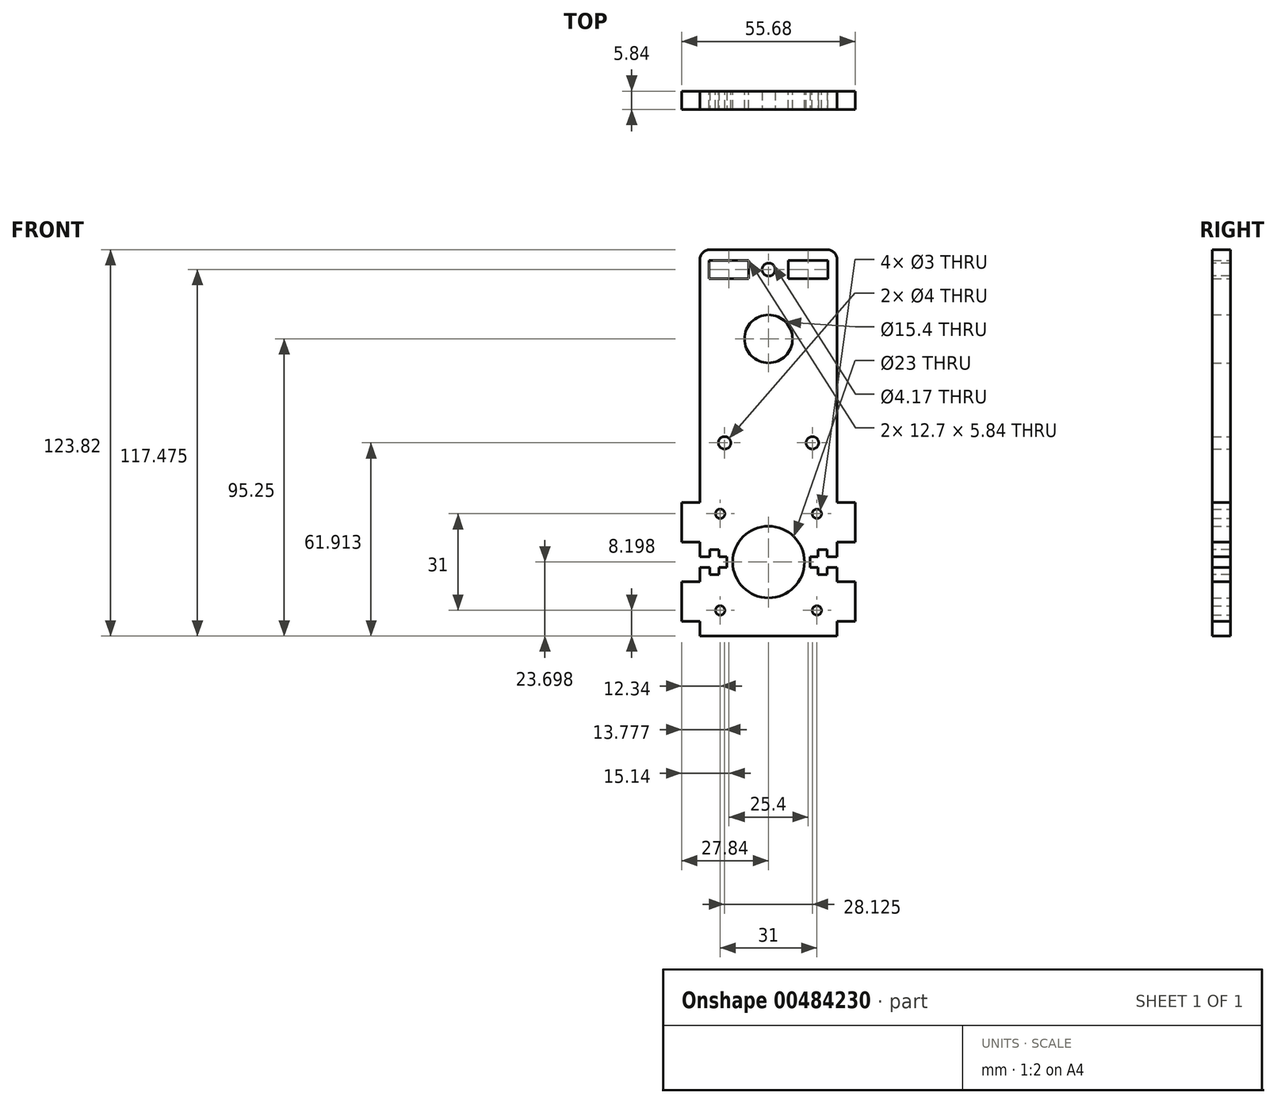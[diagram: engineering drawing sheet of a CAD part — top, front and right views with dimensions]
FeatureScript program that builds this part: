
annotation { "Feature Type Name" : "Feature", "Feature Type Description" : "" }
export const myFeature = defineFeature(function(context is Context, id is Id, definition is map)
    precondition{}
    {
        {
            var Q0;
            Q0=qCreatedBy(makeId("Front.planeOp"),FACE);
            var sketch = newSketch(context, id + "F0", { "sketchPlane" : qUnion([Q0])});
            skCircle(sketch, "E0", {"center": v(0, 0) * mm, "radius": 7.7 * mm});
            skCircle(sketch, "E1", {"center": v(0, 0) * mm, "radius": 8 * mm, "construction": true});
            skCircle(sketch, "E2", {"center": v(0, -71.55) * mm, "radius": 11.5 * mm});
            skLineSegment(sketch, "E3.bottom", {"start": v(-22, 28.58) * mm, "end": v(22, 28.58) * mm});
            skLineSegment(sketch, "E3.top", {"start": v(-22, -95.25) * mm, "end": v(22, -95.25) * mm});
            skLineSegment(sketch, "E3.right", {"start": v(22, 28.58) * mm, "end": v(22, -52.5) * mm});
            skPoint(sketch, "E3.middle", {"position": v(0, -33.34) * mm});
            skCircle(sketch, "E4", {"center": v(0, 0) * mm, "radius": 15.88 * mm, "construction": true});
            skLineSegment(sketch, "E5.bottom", {"start": v(-21.15, -50.4) * mm, "end": v(21.15, -50.4) * mm, "construction": true});
            skLineSegment(sketch, "E5.top", {"start": v(-21.15, -92.7) * mm, "end": v(21.15, -92.7) * mm, "construction": true});
            skLineSegment(sketch, "E5.left", {"start": v(-21.15, -50.4) * mm, "end": v(-21.15, -92.7) * mm, "construction": true});
            skLineSegment(sketch, "E5.right", {"start": v(21.15, -50.4) * mm, "end": v(21.15, -92.7) * mm, "construction": true});
            skLineSegment(sketch, "E6", {"start": v(-15.85, -0.97) * mm, "end": v(-11.48, -72.25) * mm, "construction": true});
            skLineSegment(sketch, "E7", {"start": v(0, 0) * mm, "end": v(0, -71.55) * mm, "construction": true});
            skLineSegment(sketch, "E8.MirrorCS", {"start": v(15.85, -0.97) * mm, "end": v(11.48, -72.25) * mm, "construction": true});
            skLineSegment(sketch, "E9", {"start": v(-21.15, -71.55) * mm, "end": v(21.15, -71.55) * mm, "construction": true});
            skLineSegment(sketch, "E10", {"start": v(0, -92.7) * mm, "end": v(0, -50.4) * mm, "construction": true});
            skCircle(sketch, "E11", {"center": v(-15.5, -56.05) * mm, "radius": 1.5 * mm});
            skCircle(sketch, "E12.MirrorC", {"center": v(15.5, -56.05) * mm, "radius": 1.5 * mm});
            skCircle(sketch, "E13.MirrorC", {"center": v(15.5, -87.05) * mm, "radius": 1.5 * mm});
            skCircle(sketch, "E14.MirrorC", {"center": v(-15.5, -87.05) * mm, "radius": 1.5 * mm});
            skLineSegment(sketch, "E15.bottom", {"start": v(-22, -77.9) * mm, "end": v(-27.84, -77.9) * mm});
            skLineSegment(sketch, "E15.top", {"start": v(-22, -90.6) * mm, "end": v(-27.84, -90.6) * mm});
            skLineSegment(sketch, "E15.right", {"start": v(-27.84, -77.9) * mm, "end": v(-27.84, -90.6) * mm});
            skPoint(sketch, "E15.middle", {"position": v(-24.92, -84.25) * mm});
            skLineSegment(sketch, "E16.MirrorCS", {"start": v(-22, -65.2) * mm, "end": v(-27.84, -65.2) * mm});
            skLineSegment(sketch, "E17.MirrorCS", {"start": v(-27.84, -65.2) * mm, "end": v(-27.84, -52.5) * mm});
            skLineSegment(sketch, "E18.MirrorCS", {"start": v(-22, -52.5) * mm, "end": v(-27.84, -52.5) * mm});
            skLineSegment(sketch, "E19.trimOffspring", {"start": v(-22, -65.2) * mm, "end": v(-22, -77.9) * mm});
            skLineSegment(sketch, "E20.trimOffspring", {"start": v(-22, -90.6) * mm, "end": v(-22, -95.25) * mm});
            skLineSegment(sketch, "E21", {"start": v(-22, -52.5) * mm, "end": v(-22, 28.58) * mm});
            skLineSegment(sketch, "E22.bottom", {"start": v(-6.35, 25.15) * mm, "end": v(-19.05, 25.15) * mm});
            skLineSegment(sketch, "E22.top", {"start": v(-6.35, 19.3) * mm, "end": v(-19.05, 19.3) * mm});
            skLineSegment(sketch, "E22.left", {"start": v(-6.35, 25.15) * mm, "end": v(-6.35, 19.3) * mm});
            skLineSegment(sketch, "E22.right", {"start": v(-19.05, 25.15) * mm, "end": v(-19.05, 19.3) * mm});
            skPoint(sketch, "E22.middle", {"position": v(-12.7, 22.23) * mm});
            skLineSegment(sketch, "E23.MirrorCS", {"start": v(6.35, 25.15) * mm, "end": v(6.35, 19.3) * mm});
            skLineSegment(sketch, "E24.MirrorCS", {"start": v(6.35, 25.15) * mm, "end": v(19.05, 25.15) * mm});
            skLineSegment(sketch, "E25.MirrorCS", {"start": v(19.05, 25.15) * mm, "end": v(19.05, 19.3) * mm});
            skLineSegment(sketch, "E26.MirrorCS", {"start": v(6.35, 19.3) * mm, "end": v(19.05, 19.3) * mm});
            skLineSegment(sketch, "E27.MirrorCS", {"start": v(22, -52.5) * mm, "end": v(27.84, -52.5) * mm});
            skLineSegment(sketch, "E28.MirrorCS", {"start": v(27.84, -65.2) * mm, "end": v(27.84, -52.5) * mm});
            skLineSegment(sketch, "E29.MirrorCS", {"start": v(22, -77.9) * mm, "end": v(27.84, -77.9) * mm});
            skLineSegment(sketch, "E30.MirrorCS", {"start": v(27.84, -77.9) * mm, "end": v(27.84, -90.6) * mm});
            skLineSegment(sketch, "E31.MirrorCS", {"start": v(22, -90.6) * mm, "end": v(27.84, -90.6) * mm});
            skLineSegment(sketch, "E32", {"start": v(27.84, -65.2) * mm, "end": v(22, -65.2) * mm});
            skLineSegment(sketch, "E33.trimOffspring", {"start": v(22, -65.2) * mm, "end": v(22, -77.9) * mm});
            skLineSegment(sketch, "E34.trimOffspring", {"start": v(22, -90.6) * mm, "end": v(22, -95.25) * mm});
            skLineSegment(sketch, "E35", {"start": v(0, -33.34) * mm, "end": v(22, -33.34) * mm, "construction": true});
            skLineSegment(sketch, "E36", {"start": v(0, -33.34) * mm, "end": v(-22, -33.34) * mm, "construction": true});
            skCircle(sketch, "E37", {"center": v(-14.06, -33.34) * mm, "radius": 2 * mm});
            skPoint(sketch, "E38", {"position": v(-13.86, -33.34) * mm});
            skCircle(sketch, "E39.MirrorC", {"center": v(14.06, -33.34) * mm, "radius": 2 * mm});
            skSolve(sketch);
        }
        {
            var Q0;
            Q0 = qSketchRegion(id + "F0", true);
            extrude(context, id + "F1", {"entities" : qUnion([Q0]), "depth" : 5.84 * mm});
        }
        {
            var Q0;
            Q0=makeQuery(id+"F1.opExtrude","SWEPT_EDGE",EDGE,{"disambiguationData":[OSD([sQuery(id+"F0.wireOp",EDGE,"E3.bottom"),sQuery(id+"F0.wireOp",EDGE,"E21")])]});
            var Q1;
            Q1=makeQuery(id+"F1.opExtrude","SWEPT_EDGE",EDGE,{"disambiguationData":[OSD([sQuery(id+"F0.wireOp",EDGE,"E3.bottom"),sQuery(id+"F0.wireOp",EDGE,"E3.right")])]});
            fillet(context, id + "F2", {"entities" : qUnion([Q0, Q1]), "radius" : 3.17 * mm, "tangentPropagation" : true, "allowEdgeOverflow" : false});
        }
        {
            var Q0;
            Q0=makeQuery(id+"F1.opExtrude","CAP_FACE",FACE,{"disambiguationData":[OSD([sQuery(id+"F0.wireOp",EDGE,"E0"),sQuery(id+"F0.wireOp",EDGE,"E2"),sQuery(id+"F0.wireOp",EDGE,"E3.bottom"),sQuery(id+"F0.wireOp",EDGE,"E3.top"),sQuery(id+"F0.wireOp",EDGE,"E3.right"),sQuery(id+"F0.wireOp",EDGE,"E12.MirrorC"),sQuery(id+"F0.wireOp",EDGE,"E11"),sQuery(id+"F0.wireOp",EDGE,"E13.MirrorC"),sQuery(id+"F0.wireOp",EDGE,"E14.MirrorC"),sQuery(id+"F0.wireOp",EDGE,"E15.bottom"),sQuery(id+"F0.wireOp",EDGE,"E15.top"),sQuery(id+"F0.wireOp",EDGE,"E15.right"),sQuery(id+"F0.wireOp",EDGE,"E16.MirrorCS"),sQuery(id+"F0.wireOp",EDGE,"E17.MirrorCS"),sQuery(id+"F0.wireOp",EDGE,"E18.MirrorCS"),sQuery(id+"F0.wireOp",EDGE,"E19.trimOffspring"),sQuery(id+"F0.wireOp",EDGE,"E20.trimOffspring"),sQuery(id+"F0.wireOp",EDGE,"E21"),sQuery(id+"F0.wireOp",EDGE,"E22.bottom"),sQuery(id+"F0.wireOp",EDGE,"E22.top"),sQuery(id+"F0.wireOp",EDGE,"E22.left"),sQuery(id+"F0.wireOp",EDGE,"E22.right"),sQuery(id+"F0.wireOp",EDGE,"E23.MirrorCS"),sQuery(id+"F0.wireOp",EDGE,"E24.MirrorCS"),sQuery(id+"F0.wireOp",EDGE,"E25.MirrorCS"),sQuery(id+"F0.wireOp",EDGE,"E26.MirrorCS"),sQuery(id+"F0.wireOp",EDGE,"E27.MirrorCS"),sQuery(id+"F0.wireOp",EDGE,"E28.MirrorCS"),sQuery(id+"F0.wireOp",EDGE,"E29.MirrorCS"),sQuery(id+"F0.wireOp",EDGE,"E30.MirrorCS"),sQuery(id+"F0.wireOp",EDGE,"E31.MirrorCS"),sQuery(id+"F0.wireOp",EDGE,"E32"),sQuery(id+"F0.wireOp",EDGE,"E33.trimOffspring"),sQuery(id+"F0.wireOp",EDGE,"E34.trimOffspring"),sQuery(id+"F0.wireOp",EDGE,"E37"),sQuery(id+"F0.wireOp",EDGE,"E39.MirrorC")])],"isStart":false});
            var sketch = newSketch(context, id + "F3", { "sketchPlane" : qUnion([Q0])});
            skLineSegment(sketch, "E40", {"start": v(-22, -71.55) * mm, "end": v(22, -71.55) * mm, "construction": true});
            skLineSegment(sketch, "E41.bottom", {"start": v(-22, -69.8) * mm, "end": v(-18.83, -69.8) * mm});
            skLineSegment(sketch, "E41.top", {"start": v(-22, -73.3) * mm, "end": v(-18.83, -73.3) * mm});
            skLineSegment(sketch, "E41.left", {"start": v(-22, -69.8) * mm, "end": v(-22, -73.3) * mm});
            skPoint(sketch, "E41.middle", {"position": v(-20.41, -71.55) * mm});
            skLineSegment(sketch, "E42.bottom", {"start": v(-18.83, -67.58) * mm, "end": v(-15.85, -67.58) * mm});
            skLineSegment(sketch, "E42.top", {"start": v(-18.83, -75.52) * mm, "end": v(-15.85, -75.52) * mm});
            skLineSegment(sketch, "E42.left", {"start": v(-18.83, -67.58) * mm, "end": v(-18.83, -69.8) * mm});
            skLineSegment(sketch, "E42.right", {"start": v(-15.85, -67.58) * mm, "end": v(-15.85, -69.8) * mm});
            skPoint(sketch, "E42.middle", {"position": v(-17.34, -71.55) * mm});
            skLineSegment(sketch, "E43.trimOffspring", {"start": v(-18.83, -73.3) * mm, "end": v(-18.83, -75.52) * mm});
            skLineSegment(sketch, "E44.bottom", {"start": v(-15.85, -69.8) * mm, "end": v(-13.35, -69.8) * mm});
            skLineSegment(sketch, "E44.top", {"start": v(-15.85, -73.3) * mm, "end": v(-13.35, -73.3) * mm});
            skLineSegment(sketch, "E44.right", {"start": v(-13.35, -69.8) * mm, "end": v(-13.35, -73.3) * mm});
            skPoint(sketch, "E44.middle", {"position": v(-14.6, -71.55) * mm});
            skLineSegment(sketch, "E45.trimOffspring", {"start": v(-15.85, -73.3) * mm, "end": v(-15.85, -75.52) * mm});
            skLineSegment(sketch, "E46", {"start": v(0, -54.52) * mm, "end": v(0, -71.55) * mm, "construction": true});
            skLineSegment(sketch, "E47.MirrorCS", {"start": v(22, -69.8) * mm, "end": v(18.82, -69.8) * mm});
            skLineSegment(sketch, "E48.MirrorCS", {"start": v(22, -73.3) * mm, "end": v(18.82, -73.3) * mm});
            skPoint(sketch, "E49.MirrorP", {"position": v(14.6, -71.55) * mm});
            skLineSegment(sketch, "E50.MirrorCS", {"start": v(22, -69.8) * mm, "end": v(22, -73.3) * mm});
            skLineSegment(sketch, "E51.MirrorCS", {"start": v(18.82, -67.58) * mm, "end": v(15.85, -67.58) * mm});
            skLineSegment(sketch, "E52.MirrorCS", {"start": v(18.82, -75.52) * mm, "end": v(15.85, -75.52) * mm});
            skLineSegment(sketch, "E53.MirrorCS", {"start": v(15.85, -67.58) * mm, "end": v(15.85, -69.8) * mm});
            skLineSegment(sketch, "E54.MirrorCS", {"start": v(18.82, -73.3) * mm, "end": v(18.82, -75.52) * mm});
            skLineSegment(sketch, "E55.MirrorCS", {"start": v(15.85, -69.8) * mm, "end": v(13.35, -69.8) * mm});
            skLineSegment(sketch, "E56.MirrorCS", {"start": v(22, -71.55) * mm, "end": v(-22, -71.55) * mm, "construction": true});
            skPoint(sketch, "E57.MirrorP", {"position": v(17.34, -71.55) * mm});
            skLineSegment(sketch, "E58.MirrorCS", {"start": v(18.82, -67.58) * mm, "end": v(18.82, -69.8) * mm});
            skPoint(sketch, "E59.MirrorP", {"position": v(20.41, -71.55) * mm});
            skLineSegment(sketch, "E60.MirrorCS", {"start": v(15.85, -73.3) * mm, "end": v(13.35, -73.3) * mm});
            skLineSegment(sketch, "E61.MirrorCS", {"start": v(15.85, -73.3) * mm, "end": v(15.85, -75.52) * mm});
            skLineSegment(sketch, "E62.MirrorCS", {"start": v(13.35, -69.8) * mm, "end": v(13.35, -73.3) * mm});
            skSolve(sketch);
        }
        {
            var Q0;
            Q0 = qSketchRegion(id + "F3", true);
            extrude(context, id + "F4", {"entities" : qUnion([Q0]), "operationType" : NewBodyOperationType.REMOVE, "endBound" : BoundingType.THROUGH_ALL, "oppositeDirection" : true, "depth" : 25.4 * mm});
        }
        {
            var Q0;
            Q0=makeQuery(id+"F1.opExtrude","CAP_FACE",FACE,{"disambiguationData":[OSD([sQuery(id+"F0.wireOp",EDGE,"E0"),sQuery(id+"F0.wireOp",EDGE,"E2"),sQuery(id+"F0.wireOp",EDGE,"E3.bottom"),sQuery(id+"F0.wireOp",EDGE,"E3.top"),sQuery(id+"F0.wireOp",EDGE,"E3.right"),sQuery(id+"F0.wireOp",EDGE,"E12.MirrorC"),sQuery(id+"F0.wireOp",EDGE,"E11"),sQuery(id+"F0.wireOp",EDGE,"E13.MirrorC"),sQuery(id+"F0.wireOp",EDGE,"E14.MirrorC"),sQuery(id+"F0.wireOp",EDGE,"E15.bottom"),sQuery(id+"F0.wireOp",EDGE,"E15.top"),sQuery(id+"F0.wireOp",EDGE,"E15.right"),sQuery(id+"F0.wireOp",EDGE,"E16.MirrorCS"),sQuery(id+"F0.wireOp",EDGE,"E17.MirrorCS"),sQuery(id+"F0.wireOp",EDGE,"E18.MirrorCS"),sQuery(id+"F0.wireOp",EDGE,"E19.trimOffspring"),sQuery(id+"F0.wireOp",EDGE,"E20.trimOffspring"),sQuery(id+"F0.wireOp",EDGE,"E21"),sQuery(id+"F0.wireOp",EDGE,"E22.bottom"),sQuery(id+"F0.wireOp",EDGE,"E22.top"),sQuery(id+"F0.wireOp",EDGE,"E22.left"),sQuery(id+"F0.wireOp",EDGE,"E22.right"),sQuery(id+"F0.wireOp",EDGE,"E23.MirrorCS"),sQuery(id+"F0.wireOp",EDGE,"E24.MirrorCS"),sQuery(id+"F0.wireOp",EDGE,"E25.MirrorCS"),sQuery(id+"F0.wireOp",EDGE,"E26.MirrorCS"),sQuery(id+"F0.wireOp",EDGE,"E27.MirrorCS"),sQuery(id+"F0.wireOp",EDGE,"E28.MirrorCS"),sQuery(id+"F0.wireOp",EDGE,"E29.MirrorCS"),sQuery(id+"F0.wireOp",EDGE,"E30.MirrorCS"),sQuery(id+"F0.wireOp",EDGE,"E31.MirrorCS"),sQuery(id+"F0.wireOp",EDGE,"E32"),sQuery(id+"F0.wireOp",EDGE,"E33.trimOffspring"),sQuery(id+"F0.wireOp",EDGE,"E34.trimOffspring"),sQuery(id+"F0.wireOp",EDGE,"E37"),sQuery(id+"F0.wireOp",EDGE,"E39.MirrorC")])],"isStart":false});
            var sketch = newSketch(context, id + "F5", { "sketchPlane" : qUnion([Q0])});
            skLineSegment(sketch, "E63", {"start": v(-6.35, 22.23) * mm, "end": v(6.35, 22.23) * mm, "construction": true});
            skCircle(sketch, "E64", {"center": v(0, 22.23) * mm, "radius": 2.08 * mm});
            skSolve(sketch);
        }
        {
            var Q0;
            Q0 = qSketchRegion(id + "F5", true);
            extrude(context, id + "F6", {"entities" : qUnion([Q0]), "operationType" : NewBodyOperationType.REMOVE, "oppositeDirection" : true, "depth" : 25.4 * mm});
        }
    });
